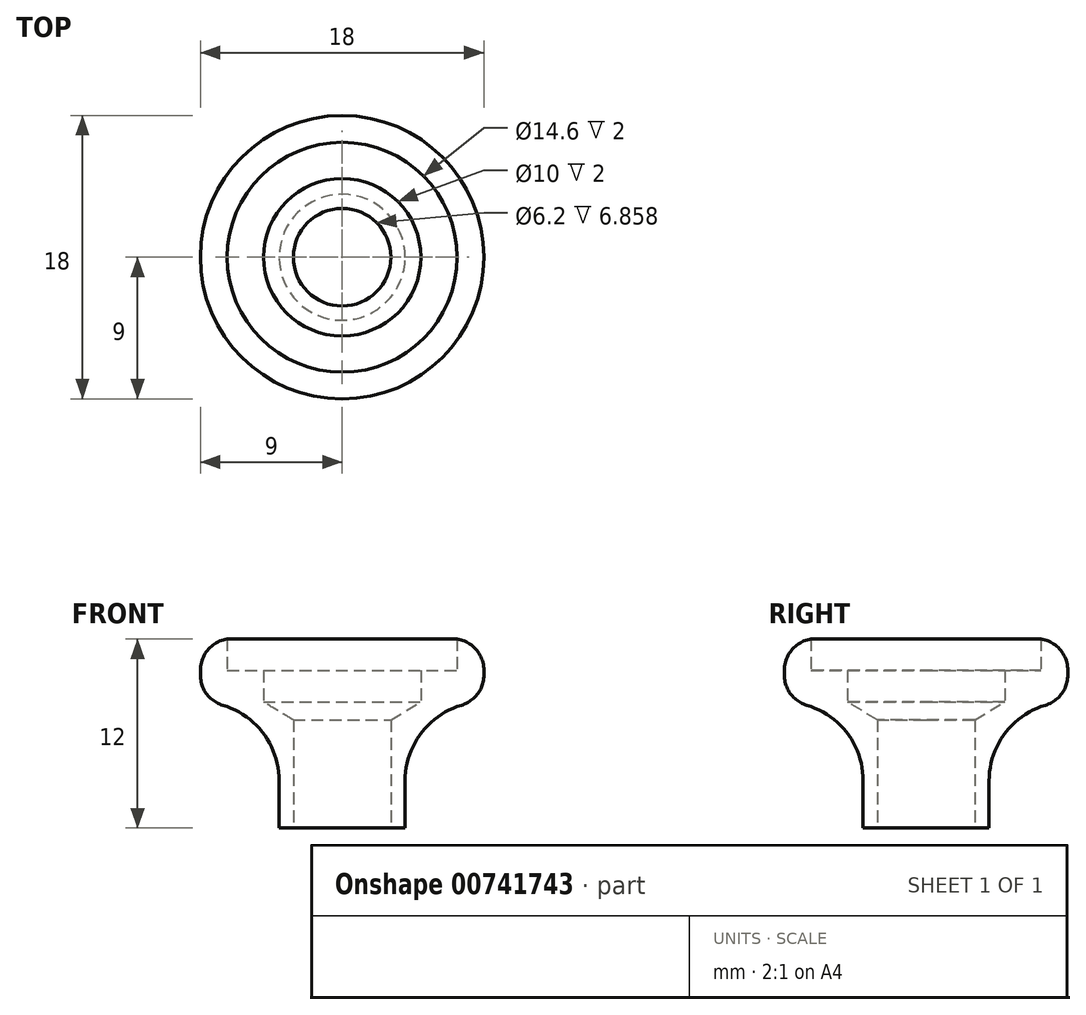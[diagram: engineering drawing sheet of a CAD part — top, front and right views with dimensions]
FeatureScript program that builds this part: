
annotation { "Feature Type Name" : "Feature", "Feature Type Description" : "" }
export const myFeature = defineFeature(function(context is Context, id is Id, definition is map)
    precondition{}
    {
        {
            var Q0;
            Q0=qCreatedBy(makeId("Front.planeOp"),FACE);
            var sketch = newSketch(context, id + "F0", { "sketchPlane" : qUnion([Q0])});
            skLineSegment(sketch, "E0", {"start": v(9, 10.02) * mm, "end": v(9, 9.7) * mm});
            skLineSegment(sketch, "E1", {"start": v(4, 3) * mm, "end": v(4, 0) * mm});
            skLineSegment(sketch, "E2", {"start": v(4, 0) * mm, "end": v(3.1, 0) * mm});
            skLineSegment(sketch, "E3", {"start": v(3.1, 6.86) * mm, "end": v(3.1, 0) * mm});
            skLineSegment(sketch, "E4", {"start": v(5, 8) * mm, "end": v(3.1, 6.86) * mm});
            skLineSegment(sketch, "E5", {"start": v(5, 10) * mm, "end": v(5, 8) * mm});
            skLineSegment(sketch, "E6", {"start": v(7.3, 10) * mm, "end": v(5, 10) * mm});
            skLineSegment(sketch, "E7", {"start": v(0, -1) * mm, "end": v(0, 13) * mm, "construction": true});
            skLineSegment(sketch, "E8", {"start": v(7.3, 12) * mm, "end": v(7.3, 10) * mm});
            skArc(sketch, "E9", {"start": v(7.57, 7.8) * mm, "mid": v(5, 5.99) * mm, "end": v(4, 3) * mm});
            skArc(sketch, "E10", {"start": v(7.57, 7.8) * mm, "mid": v(8.6, 8.51) * mm, "end": v(9, 9.7) * mm});
            skArc(sketch, "E11", {"start": v(9, 10.02) * mm, "mid": v(8.52, 11.33) * mm, "end": v(7.3, 12) * mm});
            skSolve(sketch);
        }
        {
            var Q0;
            Q0=makeQuery(id+"F0.imprint","IMPRINT",FACE,{"disambiguationData":[TD([[makeQuery(id+"F0.imprint","IMPRINT",EDGE,{"derivedFrom":sQuery(id+"F0.wireOp",EDGE,"E0")}),-1.0]])]});
            var Q1;
            Q1=sQuery(id+"F0.wireOp",EDGE,"E7");
            revolve(context, id + "F1", {"entities" : qUnion([Q0]), "axis" : qUnion([Q1]), "revolveType" : RevolveType.FULL});
        }
    });
